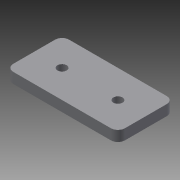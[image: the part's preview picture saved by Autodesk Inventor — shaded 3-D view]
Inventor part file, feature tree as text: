
AUTODESK INVENTOR PART (.ipt)
format: ipt  version: 2014 SP1 (Build 180222100, 222)  size: 91,648 bytes
history: native  units: in
note: dims shown in document units (in); Inventor stores cm internally (conversion verified against a paired STEP export)
features: extrude x2, sketch x2
ambient origin geometry x8: Origin, YZ Plane, XZ Plane, XY Plane, X Axis, Y Axis, Z Axis, Center Point
bodies: Solid1 (feature_tree)
feature tree (4):
  extrude  "Extrusion1"  Depth=2.0in
  extrude  "Extrusion2"  Depth=0.1875in TaperAngle=0.0deg
  sketch  "Sketch1"  dims[d0=1.0in d1=2.0in]
  sketch  "Sketch2"  dims[d2=0.125in d3=0.1875in d4=0.0in d5=0.164in d6=0.5in d7=0.5in d8=0.7874in d10=1.0in d11=0.3937in d13=1.0in d15=0.1875in d16=0.0in]
